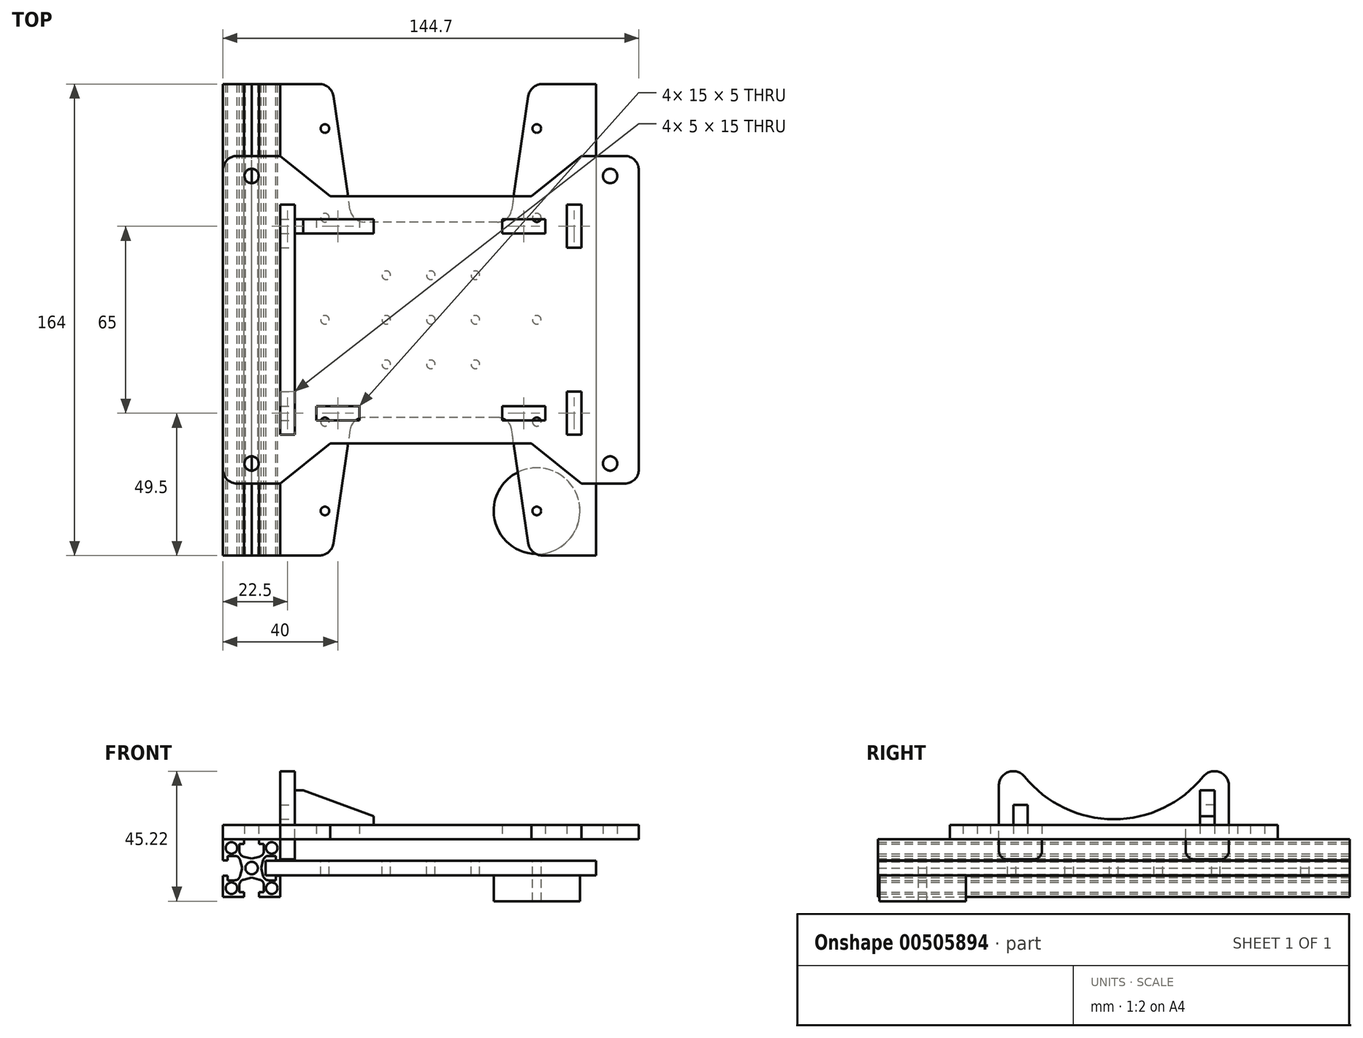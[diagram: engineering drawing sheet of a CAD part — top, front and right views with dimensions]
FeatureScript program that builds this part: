
annotation { "Feature Type Name" : "Feature", "Feature Type Description" : "" }
export const myFeature = defineFeature(function(context is Context, id is Id, definition is map)
    precondition{}
    {
        {
            var Q0;
            Q0=qCreatedBy(makeId("Top.planeOp"),FACE);
            var sketch = newSketch(context, id + "F0", { "sketchPlane" : qUnion([Q0])});
            skLineSegment(sketch, "E0.bottom", {"start": v(-72.35, 82) * mm, "end": v(72.35, 82) * mm, "construction": true});
            skLineSegment(sketch, "E0.top", {"start": v(-72.35, -82) * mm, "end": v(72.35, -82) * mm, "construction": true});
            skLineSegment(sketch, "E0.left", {"start": v(-72.35, 82) * mm, "end": v(-72.35, -82) * mm});
            skLineSegment(sketch, "E0.right", {"start": v(72.35, 82) * mm, "end": v(72.35, -82) * mm});
            skPoint(sketch, "E0.middle", {"position": v(0, 0) * mm});
            skLineSegment(sketch, "E1", {"start": v(-52.35, 82) * mm, "end": v(-52.35, -82) * mm, "construction": true});
            skLineSegment(sketch, "E2", {"start": v(52.35, 82) * mm, "end": v(52.35, -82) * mm, "construction": true});
            skLineSegment(sketch, "E3", {"start": v(72.35, 57) * mm, "end": v(-72.35, 57) * mm});
            skLineSegment(sketch, "E4", {"start": v(-72.35, -57) * mm, "end": v(72.35, -57) * mm});
            skLineSegment(sketch, "E5", {"start": v(0, 0) * mm, "end": v(30.22, 0) * mm, "construction": true});
            skLineSegment(sketch, "E6", {"start": v(0, 0) * mm, "end": v(0, -15.6) * mm, "construction": true});
            skCircle(sketch, "E7", {"center": v(62.35, 50) * mm, "radius": 2.5 * mm});
            skCircle(sketch, "E8.MirrorC", {"center": v(-62.35, 50) * mm, "radius": 2.5 * mm});
            skCircle(sketch, "E9.MirrorC", {"center": v(-62.35, -50) * mm, "radius": 2.5 * mm});
            skCircle(sketch, "E10.MirrorC", {"center": v(62.35, -50) * mm, "radius": 2.5 * mm});
            skLineSegment(sketch, "E11", {"start": v(-52.35, 57) * mm, "end": v(-35, 43) * mm});
            skLineSegment(sketch, "E12", {"start": v(-35, 43) * mm, "end": v(35, 43) * mm});
            skLineSegment(sketch, "E13", {"start": v(35, 43) * mm, "end": v(52.35, 57) * mm});
            skLineSegment(sketch, "E14", {"start": v(0, 57) * mm, "end": v(0, 43) * mm, "construction": true});
            skLineSegment(sketch, "E15.MirrorCS", {"start": v(35, -43) * mm, "end": v(52.35, -57) * mm});
            skLineSegment(sketch, "E16.MirrorCS", {"start": v(-35, -43) * mm, "end": v(35, -43) * mm});
            skLineSegment(sketch, "E17.MirrorCS", {"start": v(-52.35, -57) * mm, "end": v(-35, -43) * mm});
            skLineSegment(sketch, "E18.bottom", {"start": v(39.85, 35) * mm, "end": v(24.85, 35) * mm});
            skLineSegment(sketch, "E18.top", {"start": v(39.85, 30) * mm, "end": v(24.85, 30) * mm});
            skLineSegment(sketch, "E18.left", {"start": v(39.85, 35) * mm, "end": v(39.85, 30) * mm});
            skLineSegment(sketch, "E18.right", {"start": v(24.85, 35) * mm, "end": v(24.85, 30) * mm});
            skPoint(sketch, "E18.middle", {"position": v(32.35, 32.5) * mm});
            skLineSegment(sketch, "E19.bottom", {"start": v(52.35, 40) * mm, "end": v(47.35, 40) * mm});
            skLineSegment(sketch, "E19.top", {"start": v(52.35, 25) * mm, "end": v(47.35, 25) * mm});
            skLineSegment(sketch, "E19.left", {"start": v(52.35, 40) * mm, "end": v(52.35, 25) * mm});
            skLineSegment(sketch, "E19.right", {"start": v(47.35, 40) * mm, "end": v(47.35, 25) * mm});
            skPoint(sketch, "E19.middle", {"position": v(49.85, 32.5) * mm});
            skLineSegment(sketch, "E20.MirrorCS", {"start": v(-39.85, 35) * mm, "end": v(-24.85, 35) * mm});
            skLineSegment(sketch, "E21.MirrorCS", {"start": v(-24.85, 35) * mm, "end": v(-24.85, 30) * mm});
            skLineSegment(sketch, "E22.MirrorCS", {"start": v(-39.85, 30) * mm, "end": v(-24.85, 30) * mm});
            skLineSegment(sketch, "E23.MirrorCS", {"start": v(-39.85, 35) * mm, "end": v(-39.85, 30) * mm});
            skLineSegment(sketch, "E24.MirrorCS", {"start": v(-52.35, 40) * mm, "end": v(-47.35, 40) * mm});
            skLineSegment(sketch, "E25.MirrorCS", {"start": v(-47.35, 40) * mm, "end": v(-47.35, 25) * mm});
            skLineSegment(sketch, "E26.MirrorCS", {"start": v(-52.35, 25) * mm, "end": v(-47.35, 25) * mm});
            skLineSegment(sketch, "E27.MirrorCS", {"start": v(-39.85, -35) * mm, "end": v(-24.85, -35) * mm});
            skLineSegment(sketch, "E28.MirrorCS", {"start": v(-39.85, -35) * mm, "end": v(-39.85, -30) * mm});
            skLineSegment(sketch, "E29.MirrorCS", {"start": v(-39.85, -30) * mm, "end": v(-24.85, -30) * mm});
            skLineSegment(sketch, "E30.MirrorCS", {"start": v(-24.85, -35) * mm, "end": v(-24.85, -30) * mm});
            skLineSegment(sketch, "E31.MirrorCS", {"start": v(-52.35, -40) * mm, "end": v(-47.35, -40) * mm});
            skLineSegment(sketch, "E32.MirrorCS", {"start": v(-47.35, -40) * mm, "end": v(-47.35, -25) * mm});
            skLineSegment(sketch, "E33.MirrorCS", {"start": v(-52.35, -25) * mm, "end": v(-47.35, -25) * mm});
            skLineSegment(sketch, "E34.MirrorCS", {"start": v(39.85, -35) * mm, "end": v(24.85, -35) * mm});
            skLineSegment(sketch, "E35.MirrorCS", {"start": v(24.85, -35) * mm, "end": v(24.85, -30) * mm});
            skLineSegment(sketch, "E36.MirrorCS", {"start": v(39.85, -30) * mm, "end": v(24.85, -30) * mm});
            skLineSegment(sketch, "E37.MirrorCS", {"start": v(39.85, -35) * mm, "end": v(39.85, -30) * mm});
            skLineSegment(sketch, "E38.MirrorCS", {"start": v(52.35, -40) * mm, "end": v(47.35, -40) * mm});
            skLineSegment(sketch, "E39.MirrorCS", {"start": v(47.35, -40) * mm, "end": v(47.35, -25) * mm});
            skLineSegment(sketch, "E40.MirrorCS", {"start": v(52.35, -25) * mm, "end": v(47.35, -25) * mm});
            skLineSegment(sketch, "E41", {"start": v(-52.35, 40) * mm, "end": v(-52.35, 25) * mm});
            skLineSegment(sketch, "E42", {"start": v(-52.35, -25) * mm, "end": v(-52.35, -40) * mm});
            skLineSegment(sketch, "E43", {"start": v(52.35, -25) * mm, "end": v(52.35, -40) * mm});
            skSolve(sketch);
        }
        {
            var Q0;
            Q0=makeQuery(id+"F0.imprint","IMPRINT",FACE,{"disambiguationData":[TD([[makeQuery(id+"F0.imprint","IMPRINT",EDGE,{"derivedFrom":sQuery(id+"F0.wireOp",EDGE,"E7")}),-1.0]])]});
            extrude(context, id + "F1", {"entities" : qUnion([Q0]), "depth" : 5 * mm});
        }
        {
            var Q0;
            Q0=makeQuery(id+"F1.opExtrude","SWEPT_EDGE",EDGE,{"disambiguationData":[OSD([sQuery(id+"F0.wireOp",EDGE,"E0.left"),sQuery(id+"F0.wireOp",EDGE,"E3")])]});
            var Q1;
            Q1=makeQuery(id+"F1.opExtrude","SWEPT_EDGE",EDGE,{"disambiguationData":[OSD([sQuery(id+"F0.wireOp",EDGE,"E0.left"),sQuery(id+"F0.wireOp",EDGE,"E4")])]});
            var Q2;
            Q2=makeQuery(id+"F1.opExtrude","SWEPT_EDGE",EDGE,{"disambiguationData":[OSD([sQuery(id+"F0.wireOp",EDGE,"E0.right"),sQuery(id+"F0.wireOp",EDGE,"E4")])]});
            var Q3;
            Q3=makeQuery(id+"F1.opExtrude","SWEPT_EDGE",EDGE,{"disambiguationData":[OSD([sQuery(id+"F0.wireOp",EDGE,"E0.right"),sQuery(id+"F0.wireOp",EDGE,"E3")])]});
            fillet(context, id + "F2", {"entities" : qUnion([Q0, Q1, Q2, Q3]), "radius" : 5 * mm, "tangentPropagation" : true, "allowEdgeOverflow" : false});
        }
        {
            var Q0;
            Q0=makeQuery(id+"F1.opExtrude","SWEPT_FACE",FACE,{"disambiguationData":[OSD([sQuery(id+"F0.wireOp",EDGE,"E25.MirrorCS")])]});
            var sketch = newSketch(context, id + "F3", { "sketchPlane" : qUnion([Q0])});
            skArc(sketch, "E44", {"start": v(31.11, 21.86) * mm, "mid": v(0, 7) * mm, "end": v(-31.11, 21.86) * mm});
            skLineSegment(sketch, "E45.0", {"start": v(-40, 5) * mm, "end": v(-40, 0) * mm});
            skLineSegment(sketch, "E45.2", {"start": v(-25, 5) * mm, "end": v(-25, 0) * mm});
            skLineSegment(sketch, "E45.3", {"start": v(40, 5) * mm, "end": v(40, 0) * mm});
            skLineSegment(sketch, "E45.5", {"start": v(25, 5) * mm, "end": v(25, 0) * mm});
            skLineSegment(sketch, "E46", {"start": v(-25, 5) * mm, "end": v(25, 5) * mm});
            skLineSegment(sketch, "E47", {"start": v(-40, 18.72) * mm, "end": v(-40, 5) * mm});
            skLineSegment(sketch, "E48", {"start": v(40, 18.72) * mm, "end": v(40, 5) * mm});
            skPoint(sketch, "E49.visualSharp", {"position": v(-40, 47) * mm});
            skArc(sketch, "E49.filletArc", {"start": v(-31.11, 21.86) * mm, "mid": v(-36.67, 23.43) * mm, "end": v(-40, 18.72) * mm});
            skPoint(sketch, "E50.visualSharp", {"position": v(40, 47) * mm});
            skArc(sketch, "E50.filletArc", {"start": v(40, 18.72) * mm, "mid": v(36.67, 23.43) * mm, "end": v(31.11, 21.86) * mm});
            skLineSegment(sketch, "E51", {"start": v(-40, 0) * mm, "end": v(-40, -4) * mm});
            skLineSegment(sketch, "E52", {"start": v(-37, -7) * mm, "end": v(-28, -7) * mm});
            skLineSegment(sketch, "E53", {"start": v(-25, -4) * mm, "end": v(-25, 0) * mm});
            skLineSegment(sketch, "E54", {"start": v(25, 0) * mm, "end": v(25, -4) * mm});
            skLineSegment(sketch, "E55", {"start": v(28, -7) * mm, "end": v(37, -7) * mm});
            skLineSegment(sketch, "E56", {"start": v(40, -4) * mm, "end": v(40, 0) * mm});
            skPoint(sketch, "E57.visualSharp", {"position": v(-40, -7) * mm});
            skArc(sketch, "E57.filletArc", {"start": v(-40, -4) * mm, "mid": v(-39.12, -6.12) * mm, "end": v(-37, -7) * mm});
            skPoint(sketch, "E58.visualSharp", {"position": v(-25, -7) * mm});
            skArc(sketch, "E58.filletArc", {"start": v(-28, -7) * mm, "mid": v(-25.88, -6.12) * mm, "end": v(-25, -4) * mm});
            skPoint(sketch, "E59.visualSharp", {"position": v(25, -7) * mm});
            skArc(sketch, "E59.filletArc", {"start": v(25, -4) * mm, "mid": v(25.88, -6.12) * mm, "end": v(28, -7) * mm});
            skPoint(sketch, "E60.visualSharp", {"position": v(40, -7) * mm});
            skArc(sketch, "E60.filletArc", {"start": v(37, -7) * mm, "mid": v(39.12, -6.12) * mm, "end": v(40, -4) * mm});
            skLineSegment(sketch, "E61.bottom", {"start": v(-35, 5) * mm, "end": v(-30, 5) * mm});
            skLineSegment(sketch, "E61.top", {"start": v(-35, 12) * mm, "end": v(-30, 12) * mm});
            skLineSegment(sketch, "E61.left", {"start": v(-35, 5) * mm, "end": v(-35, 12) * mm});
            skLineSegment(sketch, "E61.right", {"start": v(-30, 5) * mm, "end": v(-30, 12) * mm});
            skPoint(sketch, "E61.middle", {"position": v(-32.5, 8.5) * mm});
            skLineSegment(sketch, "E62.bottom", {"start": v(30, 5) * mm, "end": v(35, 5) * mm});
            skLineSegment(sketch, "E62.top", {"start": v(30, 12) * mm, "end": v(35, 12) * mm});
            skLineSegment(sketch, "E62.left", {"start": v(30, 5) * mm, "end": v(30, 12) * mm});
            skLineSegment(sketch, "E62.right", {"start": v(35, 5) * mm, "end": v(35, 12) * mm});
            skPoint(sketch, "E62.middle", {"position": v(32.5, 8.5) * mm});
            skPoint(sketch, "E63", {"position": v(-32.5, -7) * mm});
            skPoint(sketch, "E64", {"position": v(32.5, -7) * mm});
            skSolve(sketch);
        }
        {
            var Q0;
            Q0 = qSketchRegion(id + "F3", true);
            extrude(context, id + "F4", {"entities" : qUnion([Q0]), "depth" : 5 * mm});
        }
        {
            var Q0;
            Q0=makeQuery(id+"F1.opExtrude","SWEPT_FACE",FACE,{"disambiguationData":[OSD([sQuery(id+"F0.wireOp",EDGE,"E22.MirrorCS")])]});
            var sketch = newSketch(context, id + "F5", { "sketchPlane" : qUnion([Q0])});
            skLineSegment(sketch, "E65.0", {"start": v(24.85, 5) * mm, "end": v(24.85, 0) * mm});
            skLineSegment(sketch, "E65.1", {"start": v(39.85, 0) * mm, "end": v(24.85, 0) * mm});
            skLineSegment(sketch, "E65.2", {"start": v(39.85, 5) * mm, "end": v(39.85, 0) * mm});
            skLineSegment(sketch, "E65.3", {"start": v(52.35, 5) * mm, "end": v(47.35, 5) * mm});
            skLineSegment(sketch, "E65.4", {"start": v(52.35, 5) * mm, "end": v(52.35, 12) * mm});
            skLineSegment(sketch, "E65.5", {"start": v(52.35, 12) * mm, "end": v(47.35, 12) * mm});
            skLineSegment(sketch, "E66", {"start": v(39.85, 5) * mm, "end": v(47.35, 5) * mm});
            skLineSegment(sketch, "E67", {"start": v(47.35, 12) * mm, "end": v(47.35, 17) * mm});
            skLineSegment(sketch, "E68", {"start": v(47.35, 17) * mm, "end": v(44.35, 17) * mm});
            skLineSegment(sketch, "E69", {"start": v(44.35, 17) * mm, "end": v(19.85, 8) * mm});
            skLineSegment(sketch, "E70", {"start": v(19.85, 8) * mm, "end": v(19.85, 5) * mm});
            skLineSegment(sketch, "E71", {"start": v(19.85, 5) * mm, "end": v(24.85, 5) * mm});
            skSolve(sketch);
        }
        {
            var Q0;
            Q0 = qSketchRegion(id + "F5", true);
            extrude(context, id + "F6", {"entities" : qUnion([Q0]), "depth" : 5 * mm});
        }
        {
            var Q0;
            Q0=qCreatedBy(makeId("Front.planeOp"),FACE);
            var sketch = newSketch(context, id + "F7", { "sketchPlane" : qUnion([Q0])});
            skLineSegment(sketch, "E72.bottom", {"start": v(-52.35, 0) * mm, "end": v(-72.35, 0) * mm});
            skLineSegment(sketch, "E72.top", {"start": v(-52.35, -20) * mm, "end": v(-72.35, -20) * mm});
            skLineSegment(sketch, "E72.left", {"start": v(-52.35, 0) * mm, "end": v(-52.35, -20) * mm});
            skLineSegment(sketch, "E72.right", {"start": v(-72.35, 0) * mm, "end": v(-72.35, -20) * mm});
            skPoint(sketch, "E72.middle", {"position": v(-62.35, -10) * mm});
            skCircle(sketch, "E73", {"center": v(-62.35, -10) * mm, "radius": 2.15 * mm});
            skLineSegment(sketch, "E74", {"start": v(-62.35, 0) * mm, "end": v(-62.35, -20) * mm, "construction": true});
            skLineSegment(sketch, "E75", {"start": v(-52.35, -10) * mm, "end": v(-72.35, -10) * mm, "construction": true});
            skLineSegment(sketch, "E76", {"start": v(-52.35, 0) * mm, "end": v(-62.35, -10) * mm, "construction": true});
            skCircle(sketch, "E77", {"center": v(-55.35, -3) * mm, "radius": 2 * mm});
            skLineSegment(sketch, "E78", {"start": v(-59.72, 0) * mm, "end": v(-59.72, -1.63) * mm});
            skLineSegment(sketch, "E79", {"start": v(-59.72, -1.63) * mm, "end": v(-58.1, -1.63) * mm});
            skLineSegment(sketch, "E80", {"start": v(-58.1, -1.63) * mm, "end": v(-58.1, -4.07) * mm});
            skLineSegment(sketch, "E81", {"start": v(-59.6, -6) * mm, "end": v(-62.35, -6.7) * mm});
            skPoint(sketch, "E82.visualSharp", {"position": v(-58.1, -5.62) * mm});
            skArc(sketch, "E82.filletArc", {"start": v(-59.6, -6) * mm, "mid": v(-58.52, -5.3) * mm, "end": v(-58.1, -4.07) * mm});
            skLineSegment(sketch, "E83.MirrorCS", {"start": v(-52.35, -7.37) * mm, "end": v(-53.97, -7.37) * mm});
            skLineSegment(sketch, "E84.MirrorCS", {"start": v(-53.97, -7.37) * mm, "end": v(-53.97, -5.75) * mm});
            skLineSegment(sketch, "E85.MirrorCS", {"start": v(-53.97, -5.75) * mm, "end": v(-56.42, -5.75) * mm});
            skArc(sketch, "E86.MirrorCS", {"start": v(-58.36, -7.26) * mm, "mid": v(-57.65, -6.17) * mm, "end": v(-56.42, -5.75) * mm});
            skLineSegment(sketch, "E87.MirrorCS", {"start": v(-58.36, -7.26) * mm, "end": v(-59.05, -10) * mm});
            skLineSegment(sketch, "E88.MirrorCS", {"start": v(-64.97, 0) * mm, "end": v(-64.97, -1.63) * mm});
            skLineSegment(sketch, "E89.MirrorCS", {"start": v(-64.97, -1.63) * mm, "end": v(-66.6, -1.63) * mm});
            skLineSegment(sketch, "E90.MirrorCS", {"start": v(-66.6, -1.63) * mm, "end": v(-66.6, -4.07) * mm});
            skArc(sketch, "E91.MirrorCS", {"start": v(-65.1, -6) * mm, "mid": v(-66.18, -5.3) * mm, "end": v(-66.6, -4.07) * mm});
            skLineSegment(sketch, "E92.MirrorCS", {"start": v(-65.1, -6) * mm, "end": v(-62.35, -6.7) * mm});
            skLineSegment(sketch, "E93.MirrorCS", {"start": v(-66.34, -7.26) * mm, "end": v(-65.65, -10) * mm});
            skArc(sketch, "E94.MirrorCS", {"start": v(-66.34, -7.26) * mm, "mid": v(-67.05, -6.17) * mm, "end": v(-68.28, -5.75) * mm});
            skLineSegment(sketch, "E95.MirrorCS", {"start": v(-70.72, -5.75) * mm, "end": v(-68.28, -5.75) * mm});
            skLineSegment(sketch, "E96.MirrorCS", {"start": v(-70.72, -7.37) * mm, "end": v(-70.72, -5.75) * mm});
            skLineSegment(sketch, "E97.MirrorCS", {"start": v(-72.35, -7.37) * mm, "end": v(-70.72, -7.37) * mm});
            skLineSegment(sketch, "E98.MirrorCS", {"start": v(-66.34, -12.74) * mm, "end": v(-65.65, -10) * mm});
            skArc(sketch, "E99.MirrorCS", {"start": v(-66.34, -12.74) * mm, "mid": v(-67.05, -13.83) * mm, "end": v(-68.28, -14.25) * mm});
            skLineSegment(sketch, "E100.MirrorCS", {"start": v(-70.72, -14.25) * mm, "end": v(-68.28, -14.25) * mm});
            skLineSegment(sketch, "E101.MirrorCS", {"start": v(-70.72, -12.63) * mm, "end": v(-70.72, -14.25) * mm});
            skLineSegment(sketch, "E102.MirrorCS", {"start": v(-72.35, -12.63) * mm, "end": v(-70.72, -12.63) * mm});
            skLineSegment(sketch, "E103.MirrorCS", {"start": v(-58.36, -12.74) * mm, "end": v(-59.05, -10) * mm});
            skArc(sketch, "E104.MirrorCS", {"start": v(-58.36, -12.74) * mm, "mid": v(-57.65, -13.83) * mm, "end": v(-56.42, -14.25) * mm});
            skLineSegment(sketch, "E105.MirrorCS", {"start": v(-53.97, -14.25) * mm, "end": v(-56.42, -14.25) * mm});
            skLineSegment(sketch, "E106.MirrorCS", {"start": v(-53.97, -12.63) * mm, "end": v(-53.97, -14.25) * mm});
            skLineSegment(sketch, "E107.MirrorCS", {"start": v(-52.35, -12.63) * mm, "end": v(-53.97, -12.63) * mm});
            skLineSegment(sketch, "E108.MirrorCS", {"start": v(-59.72, -20) * mm, "end": v(-59.72, -18.37) * mm});
            skLineSegment(sketch, "E109.MirrorCS", {"start": v(-59.72, -18.38) * mm, "end": v(-58.1, -18.38) * mm});
            skLineSegment(sketch, "E110.MirrorCS", {"start": v(-58.1, -18.37) * mm, "end": v(-58.1, -15.93) * mm});
            skArc(sketch, "E111.MirrorCS", {"start": v(-59.6, -14) * mm, "mid": v(-58.52, -14.7) * mm, "end": v(-58.1, -15.93) * mm});
            skLineSegment(sketch, "E112.MirrorCS", {"start": v(-59.6, -14) * mm, "end": v(-62.35, -13.3) * mm});
            skLineSegment(sketch, "E113.MirrorCS", {"start": v(-65.1, -14) * mm, "end": v(-62.35, -13.3) * mm});
            skArc(sketch, "E114.MirrorCS", {"start": v(-65.1, -14) * mm, "mid": v(-66.18, -14.7) * mm, "end": v(-66.6, -15.93) * mm});
            skLineSegment(sketch, "E115.MirrorCS", {"start": v(-66.6, -18.37) * mm, "end": v(-66.6, -15.93) * mm});
            skLineSegment(sketch, "E116.MirrorCS", {"start": v(-64.97, -18.38) * mm, "end": v(-66.6, -18.38) * mm});
            skLineSegment(sketch, "E117.MirrorCS", {"start": v(-64.97, -20) * mm, "end": v(-64.97, -18.37) * mm});
            skCircle(sketch, "E118.1.0", {"center": v(-69.35, -3) * mm, "radius": 2 * mm});
            skCircle(sketch, "E118.2.0", {"center": v(-69.35, -17) * mm, "radius": 2 * mm});
            skCircle(sketch, "E118.3.0", {"center": v(-55.35, -17) * mm, "radius": 2 * mm});
            skSolve(sketch);
        }
        {
            var Q0;
            Q0=makeQuery(id+"F7.imprint","IMPRINT",FACE,{"disambiguationData":[TD([[makeQuery(id+"F7.imprint","IMPRINT",EDGE,{"derivedFrom":sQuery(id+"F7.wireOp",EDGE,"E73")}),-1.0]])]});
            extrude(context, id + "F8", {"entities" : qUnion([Q0]), "depth" : 82 * mm, "hasSecondDirection" : true, "secondDirectionOppositeDirection" : true, "secondDirectionDepth" : 82 * mm});
        }
        {
            var Q0;
            Q0=makeQuery(id+"F1.opExtrude","CAP_FACE",FACE,{"disambiguationData":[OSD([sQuery(id+"F0.wireOp",EDGE,"E0.left"),sQuery(id+"F0.wireOp",EDGE,"E0.right"),sQuery(id+"F0.wireOp",EDGE,"E3"),sQuery(id+"F0.wireOp",EDGE,"E4"),sQuery(id+"F0.wireOp",EDGE,"E7"),sQuery(id+"F0.wireOp",EDGE,"E8.MirrorC"),sQuery(id+"F0.wireOp",EDGE,"E9.MirrorC"),sQuery(id+"F0.wireOp",EDGE,"E10.MirrorC"),sQuery(id+"F0.wireOp",EDGE,"E11"),sQuery(id+"F0.wireOp",EDGE,"E12"),sQuery(id+"F0.wireOp",EDGE,"E13"),sQuery(id+"F0.wireOp",EDGE,"E15.MirrorCS"),sQuery(id+"F0.wireOp",EDGE,"E16.MirrorCS"),sQuery(id+"F0.wireOp",EDGE,"E17.MirrorCS"),sQuery(id+"F0.wireOp",EDGE,"E18.bottom"),sQuery(id+"F0.wireOp",EDGE,"E18.top"),sQuery(id+"F0.wireOp",EDGE,"E18.left"),sQuery(id+"F0.wireOp",EDGE,"E18.right"),sQuery(id+"F0.wireOp",EDGE,"E19.bottom"),sQuery(id+"F0.wireOp",EDGE,"E19.top"),sQuery(id+"F0.wireOp",EDGE,"E19.left"),sQuery(id+"F0.wireOp",EDGE,"E19.right"),sQuery(id+"F0.wireOp",EDGE,"E20.MirrorCS"),sQuery(id+"F0.wireOp",EDGE,"E21.MirrorCS"),sQuery(id+"F0.wireOp",EDGE,"E22.MirrorCS"),sQuery(id+"F0.wireOp",EDGE,"E23.MirrorCS"),sQuery(id+"F0.wireOp",EDGE,"E24.MirrorCS"),sQuery(id+"F0.wireOp",EDGE,"E25.MirrorCS"),sQuery(id+"F0.wireOp",EDGE,"E26.MirrorCS"),sQuery(id+"F0.wireOp",EDGE,"E27.MirrorCS"),sQuery(id+"F0.wireOp",EDGE,"E28.MirrorCS"),sQuery(id+"F0.wireOp",EDGE,"E29.MirrorCS"),sQuery(id+"F0.wireOp",EDGE,"E30.MirrorCS"),sQuery(id+"F0.wireOp",EDGE,"E31.MirrorCS"),sQuery(id+"F0.wireOp",EDGE,"E32.MirrorCS"),sQuery(id+"F0.wireOp",EDGE,"E33.MirrorCS"),sQuery(id+"F0.wireOp",EDGE,"E34.MirrorCS"),sQuery(id+"F0.wireOp",EDGE,"E35.MirrorCS"),sQuery(id+"F0.wireOp",EDGE,"E36.MirrorCS"),sQuery(id+"F0.wireOp",EDGE,"E37.MirrorCS"),sQuery(id+"F0.wireOp",EDGE,"E38.MirrorCS"),sQuery(id+"F0.wireOp",EDGE,"E39.MirrorCS"),sQuery(id+"F0.wireOp",EDGE,"E40.MirrorCS"),sQuery(id+"F0.wireOp",EDGE,"E41"),sQuery(id+"F0.wireOp",EDGE,"E42"),sQuery(id+"F0.wireOp",EDGE,"E43")])],"isStart":true});
            cPlane(context, id + "F9", {"entities" : qUnion([Q0]), "cplaneType" : CPlaneType.OFFSET, "offset" : 10 * mm, "width" : 150 * mm, "height" : 150 * mm});
        }
        {
            var Q0;
            Q0=qCreatedBy(id+"F9.planeOp",FACE);
            var sketch = newSketch(context, id + "F10", { "sketchPlane" : qUnion([Q0])});
            skLineSegment(sketch, "E119.bottom", {"start": v(15.5, -15.5) * mm, "end": v(-15.5, -15.5) * mm, "construction": true});
            skLineSegment(sketch, "E119.top", {"start": v(15.5, 15.5) * mm, "end": v(-15.5, 15.5) * mm, "construction": true});
            skLineSegment(sketch, "E119.left", {"start": v(15.5, -15.5) * mm, "end": v(15.5, 15.5) * mm, "construction": true});
            skLineSegment(sketch, "E119.right", {"start": v(-15.5, -15.5) * mm, "end": v(-15.5, 15.5) * mm, "construction": true});
            skPoint(sketch, "E119.middle", {"position": v(0, 0) * mm});
            skCircle(sketch, "E120", {"center": v(15.5, -15.5) * mm, "radius": 1.5 * mm});
            skCircle(sketch, "E121", {"center": v(0, -15.5) * mm, "radius": 1.5 * mm});
            skCircle(sketch, "E122", {"center": v(-15.5, -15.5) * mm, "radius": 1.5 * mm});
            skCircle(sketch, "E123", {"center": v(0, 0) * mm, "radius": 1.5 * mm});
            skCircle(sketch, "E124", {"center": v(15.5, 0) * mm, "radius": 1.5 * mm});
            skCircle(sketch, "E125", {"center": v(-15.5, 0) * mm, "radius": 1.5 * mm});
            skCircle(sketch, "E126", {"center": v(0, 15.5) * mm, "radius": 1.5 * mm});
            skCircle(sketch, "E127", {"center": v(15.5, 15.5) * mm, "radius": 1.5 * mm});
            skCircle(sketch, "E128", {"center": v(-15.5, 15.5) * mm, "radius": 1.5 * mm});
            skLineSegment(sketch, "E129.bottom", {"start": v(57.5, -82) * mm, "end": v(-57.5, -82) * mm});
            skLineSegment(sketch, "E129.top", {"start": v(57.5, 82) * mm, "end": v(-57.5, 82) * mm});
            skLineSegment(sketch, "E129.left", {"start": v(57.5, -82) * mm, "end": v(57.5, 82) * mm});
            skLineSegment(sketch, "E129.right", {"start": v(-57.5, -82) * mm, "end": v(-57.5, 82) * mm});
            skLineSegment(sketch, "E130", {"start": v(0, 0) * mm, "end": v(-26.6, 0) * mm, "construction": true});
            skLineSegment(sketch, "E131", {"start": v(0, 0) * mm, "end": v(0, 23.12) * mm, "construction": true});
            skLineSegment(sketch, "E132", {"start": v(34.5, -82) * mm, "end": v(28.12, -38.28) * mm});
            skLineSegment(sketch, "E133", {"start": v(23.18, -34) * mm, "end": v(-23.18, -34) * mm});
            skLineSegment(sketch, "E134", {"start": v(-28.12, -38.28) * mm, "end": v(-34.5, -82) * mm});
            skPoint(sketch, "E135", {"position": v(0, -34) * mm});
            skPoint(sketch, "E136.visualSharp", {"position": v(27.5, -34) * mm});
            skArc(sketch, "E136.filletArc", {"start": v(28.12, -38.28) * mm, "mid": v(26.45, -35.22) * mm, "end": v(23.18, -34) * mm});
            skPoint(sketch, "E137.visualSharp", {"position": v(-27.5, -34) * mm});
            skArc(sketch, "E137.filletArc", {"start": v(-23.18, -34) * mm, "mid": v(-26.45, -35.22) * mm, "end": v(-28.12, -38.28) * mm});
            skLineSegment(sketch, "E138.MirrorCS", {"start": v(-28.12, 38.28) * mm, "end": v(-34.5, 82) * mm});
            skArc(sketch, "E139.MirrorCS", {"start": v(-23.18, 34) * mm, "mid": v(-26.45, 35.22) * mm, "end": v(-28.12, 38.28) * mm});
            skLineSegment(sketch, "E140.MirrorCS", {"start": v(23.18, 34) * mm, "end": v(-23.18, 34) * mm});
            skArc(sketch, "E141.MirrorCS", {"start": v(28.12, 38.28) * mm, "mid": v(26.45, 35.22) * mm, "end": v(23.18, 34) * mm});
            skLineSegment(sketch, "E142.MirrorCS", {"start": v(34.5, 82) * mm, "end": v(28.12, 38.28) * mm});
            skCircle(sketch, "E143", {"center": v(-36.85, -66.5) * mm, "radius": 1.5 * mm});
            skCircle(sketch, "E144", {"center": v(-36.85, -35.5) * mm, "radius": 1.5 * mm});
            skCircle(sketch, "E145", {"center": v(-36.85, 0) * mm, "radius": 1.5 * mm});
            skCircle(sketch, "E146.MirrorC", {"center": v(36.85, -35.5) * mm, "radius": 1.5 * mm});
            skCircle(sketch, "E147.MirrorC", {"center": v(36.85, -66.5) * mm, "radius": 1.5 * mm});
            skCircle(sketch, "E148.MirrorC", {"center": v(36.85, 0) * mm, "radius": 1.5 * mm});
            skCircle(sketch, "E149.MirrorC", {"center": v(36.85, 35.5) * mm, "radius": 1.5 * mm});
            skCircle(sketch, "E150.MirrorC", {"center": v(36.85, 66.5) * mm, "radius": 1.5 * mm});
            skCircle(sketch, "E151.MirrorC", {"center": v(-36.85, 66.5) * mm, "radius": 1.5 * mm});
            skCircle(sketch, "E152.MirrorC", {"center": v(-36.85, 35.5) * mm, "radius": 1.5 * mm});
            skSolve(sketch);
        }
        {
            var Q0;
            Q0=makeQuery(id+"F10.imprint","IMPRINT",FACE,{"disambiguationData":[TD([[makeQuery(id+"F10.imprint","IMPRINT",EDGE,{"derivedFrom":sQuery(id+"F10.wireOp",EDGE,"E120")}),-1.0]])]});
            extrude(context, id + "F11", {"entities" : qUnion([Q0]), "depth" : 2.5 * mm, "hasSecondDirection" : true, "secondDirectionOppositeDirection" : true, "secondDirectionDepth" : 2.5 * mm});
        }
        {
            var Q0;
            Q0=makeQuery(id+"F11.opExtrude","SWEPT_EDGE",EDGE,{"disambiguationData":[OSD([sQuery(id+"F10.wireOp",EDGE,"E129.bottom"),sQuery(id+"F10.wireOp",EDGE,"E132")])]});
            var Q1;
            Q1=makeQuery(id+"F11.opExtrude","SWEPT_EDGE",EDGE,{"disambiguationData":[OSD([sQuery(id+"F10.wireOp",EDGE,"E129.bottom"),sQuery(id+"F10.wireOp",EDGE,"E134")])]});
            var Q2;
            Q2=makeQuery(id+"F11.opExtrude","SWEPT_EDGE",EDGE,{"disambiguationData":[OSD([sQuery(id+"F10.wireOp",EDGE,"E129.top"),sQuery(id+"F10.wireOp",EDGE,"E138.MirrorCS")])]});
            var Q3;
            Q3=makeQuery(id+"F11.opExtrude","SWEPT_EDGE",EDGE,{"disambiguationData":[OSD([sQuery(id+"F10.wireOp",EDGE,"E129.top"),sQuery(id+"F10.wireOp",EDGE,"E142.MirrorCS")])]});
            fillet(context, id + "F12", {"entities" : qUnion([Q0, Q1, Q2, Q3]), "radius" : 5 * mm, "tangentPropagation" : true, "allowEdgeOverflow" : false});
        }
        {
            var Q0;
            Q0=makeQuery(id+"F11.opExtrude","CAP_FACE",FACE,{"disambiguationData":[OSD([sQuery(id+"F10.wireOp",EDGE,"E120"),sQuery(id+"F10.wireOp",EDGE,"E121"),sQuery(id+"F10.wireOp",EDGE,"E122"),sQuery(id+"F10.wireOp",EDGE,"E123"),sQuery(id+"F10.wireOp",EDGE,"E124"),sQuery(id+"F10.wireOp",EDGE,"E125"),sQuery(id+"F10.wireOp",EDGE,"E126"),sQuery(id+"F10.wireOp",EDGE,"E127"),sQuery(id+"F10.wireOp",EDGE,"E128"),sQuery(id+"F10.wireOp",EDGE,"E129.bottom"),sQuery(id+"F10.wireOp",EDGE,"E129.top"),sQuery(id+"F10.wireOp",EDGE,"E129.left"),sQuery(id+"F10.wireOp",EDGE,"E129.right"),sQuery(id+"F10.wireOp",EDGE,"E132"),sQuery(id+"F10.wireOp",EDGE,"E133"),sQuery(id+"F10.wireOp",EDGE,"E134"),sQuery(id+"F10.wireOp",EDGE,"E136.filletArc"),sQuery(id+"F10.wireOp",EDGE,"E137.filletArc"),sQuery(id+"F10.wireOp",EDGE,"E138.MirrorCS"),sQuery(id+"F10.wireOp",EDGE,"E139.MirrorCS"),sQuery(id+"F10.wireOp",EDGE,"E140.MirrorCS"),sQuery(id+"F10.wireOp",EDGE,"E141.MirrorCS"),sQuery(id+"F10.wireOp",EDGE,"E142.MirrorCS"),sQuery(id+"F10.wireOp",EDGE,"E143"),sQuery(id+"F10.wireOp",EDGE,"E144"),sQuery(id+"F10.wireOp",EDGE,"E145"),sQuery(id+"F10.wireOp",EDGE,"E146.MirrorC"),sQuery(id+"F10.wireOp",EDGE,"E147.MirrorC"),sQuery(id+"F10.wireOp",EDGE,"E148.MirrorC"),sQuery(id+"F10.wireOp",EDGE,"E149.MirrorC"),sQuery(id+"F10.wireOp",EDGE,"E150.MirrorC"),sQuery(id+"F10.wireOp",EDGE,"E151.MirrorC"),sQuery(id+"F10.wireOp",EDGE,"E152.MirrorC")])],"isStart":false});
            var sketch = newSketch(context, id + "F13", { "sketchPlane" : qUnion([Q0])});
            skCircle(sketch, "E153.0", {"center": v(36.85, 66.5) * mm, "radius": 1.5 * mm});
            skCircle(sketch, "E154", {"center": v(36.85, 66.5) * mm, "radius": 15 * mm});
            skSolve(sketch);
        }
        {
            var Q0;
            Q0 = qSketchRegion(id + "F13", true);
            extrude(context, id + "F14", {"entities" : qUnion([Q0]), "depth" : 9 * mm});
        }
    });
